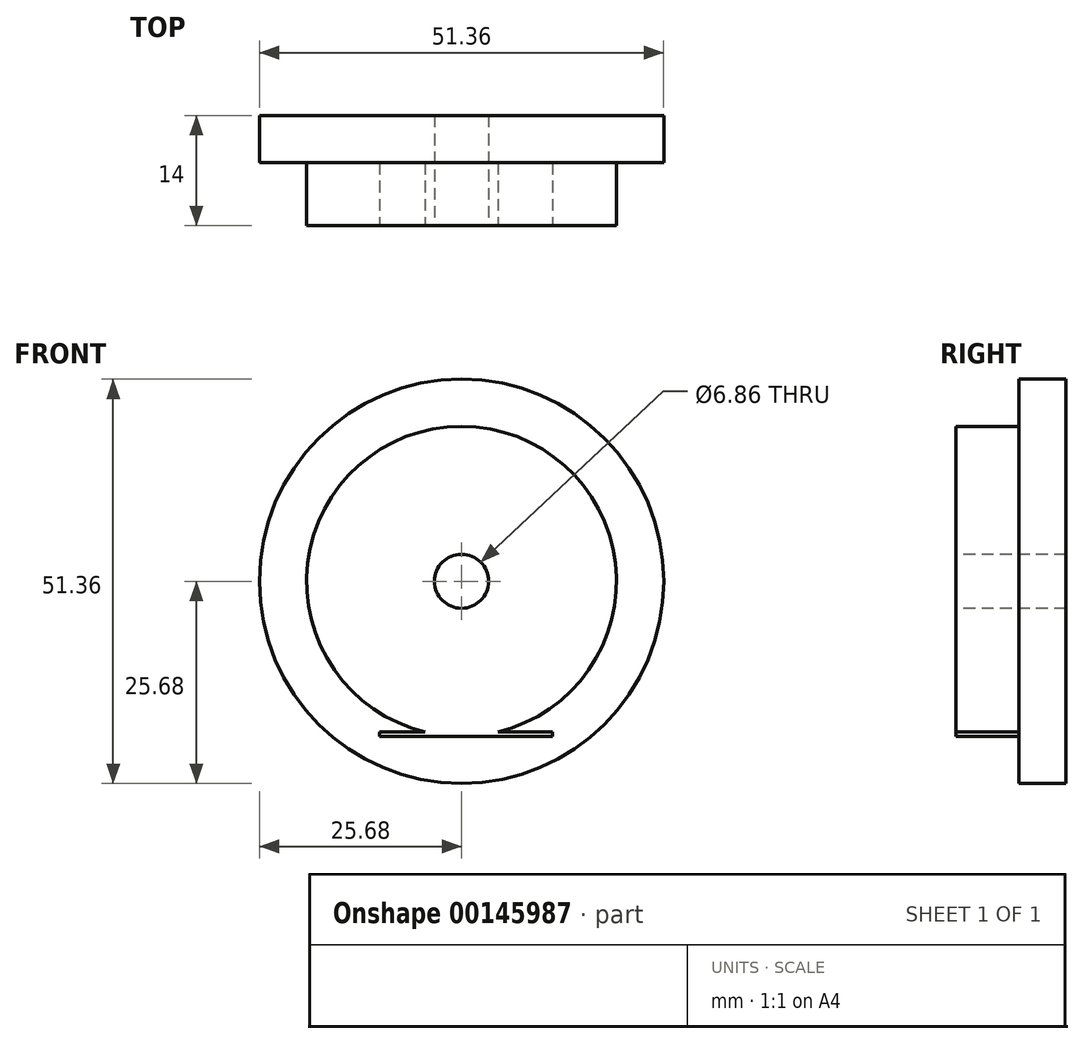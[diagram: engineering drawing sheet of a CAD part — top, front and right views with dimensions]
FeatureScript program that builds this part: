
annotation { "Feature Type Name" : "Feature", "Feature Type Description" : "" }
export const myFeature = defineFeature(function(context is Context, id is Id, definition is map)
    precondition{}
    {
        {
            var Q0;
            Q0=qCreatedBy(makeId("Right.planeOp"),FACE);
            var sketch = newSketch(context, id + "F0", { "sketchPlane" : qUnion([Q0])});
            skLineSegment(sketch, "E0", {"start": v(0, 0) * mm, "end": v(0, 25.68) * mm});
            skLineSegment(sketch, "E1", {"start": v(0, 25.68) * mm, "end": v(-6, 25.68) * mm});
            skLineSegment(sketch, "E2", {"start": v(-6, 25.68) * mm, "end": v(-6, 19.68) * mm});
            skLineSegment(sketch, "E3", {"start": v(-6, 19.68) * mm, "end": v(-14, 19.68) * mm});
            skLineSegment(sketch, "E4", {"start": v(-14, 19.68) * mm, "end": v(-14, 0) * mm});
            skLineSegment(sketch, "E5", {"start": v(-14, 0) * mm, "end": v(0, 0) * mm});
            skLineSegment(sketch, "E6", {"start": v(0, 3.43) * mm, "end": v(-14, 3.43) * mm});
            skSolve(sketch);
        }
        {
            var Q0;
            {var subQ1=sQuery(id+"F0.wireOp",EDGE,"E1");Q0=makeQuery(id+"F0.imprint","IMPRINT",FACE,{"disambiguationData":[TD([[makeQuery(id+"F0.imprint","IMPRINT",EDGE,{"derivedFrom":subQ1}),1.0]])]});}
            var Q1;
            Q1=sQuery(id+"F0.wireOp",EDGE,"E5");
            revolve(context, id + "F1", {"entities" : qUnion([Q0]), "axis" : qUnion([Q1]), "revolveType" : RevolveType.FULL});
        }
        {
            var Q0;
            Q0=makeQuery(id+"F1.opRevolve","SWEPT_FACE",FACE,{"disambiguationData":[OSD([sQuery(id+"F0.wireOp",EDGE,"E4")])]});
            var sketch = newSketch(context, id + "F2", { "sketchPlane" : qUnion([Q0])});
            skLineSegment(sketch, "E7", {"start": v(0, -19.68) * mm, "end": v(-10.44, -19.68) * mm});
            skLineSegment(sketch, "E8", {"start": v(0, -19.68) * mm, "end": v(11.58, -19.68) * mm});
            skLineSegment(sketch, "E9", {"start": v(11.58, -19.14) * mm, "end": v(11.58, -19.68) * mm});
            skLineSegment(sketch, "E10", {"start": v(11.58, -19.14) * mm, "end": v(-10.44, -19.14) * mm});
            skLineSegment(sketch, "E11", {"start": v(-10.44, -19.68) * mm, "end": v(-10.44, -19.14) * mm});
            skSolve(sketch);
        }
        {
            var Q0;
            Q0 = qSketchRegion(id + "F2", true);
            var Q1;
            Q1=makeQuery(id+"F1.opRevolve","SWEPT_FACE",FACE,{"disambiguationData":[OSD([sQuery(id+"F0.wireOp",EDGE,"E2")])]});
            extrude(context, id + "F3", {"entities" : qUnion([Q0]), "operationType" : NewBodyOperationType.ADD, "oppositeDirection" : true, "endBoundEntityFace" : qUnion([Q1]), "depth" : 10 * mm});
        }
    });
